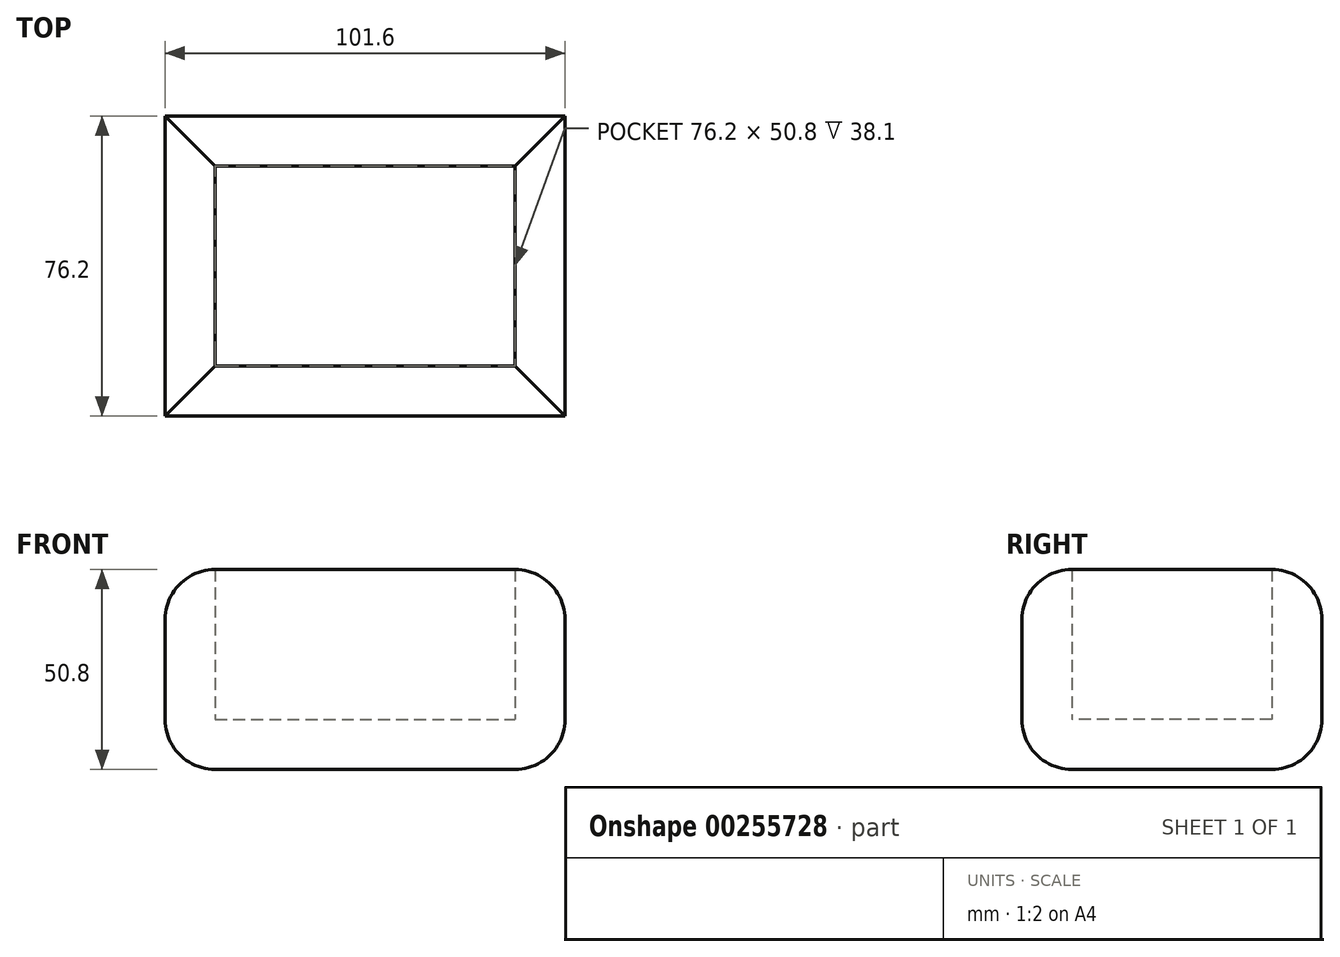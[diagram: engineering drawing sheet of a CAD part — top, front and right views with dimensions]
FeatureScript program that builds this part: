
annotation { "Feature Type Name" : "Feature", "Feature Type Description" : "" }
export const myFeature = defineFeature(function(context is Context, id is Id, definition is map)
    precondition{}
    {
        {
            var Q0;
            Q0=qCreatedBy(makeId("Top.planeOp"),FACE);
            var sketch = newSketch(context, id + "F0", { "sketchPlane" : qUnion([Q0])});
            skLineSegment(sketch, "E0", {"start": v(-52.15, 25.23) * mm, "end": v(49.45, 25.23) * mm});
            skLineSegment(sketch, "E1", {"start": v(49.45, 25.23) * mm, "end": v(49.45, -50.97) * mm});
            skLineSegment(sketch, "E2", {"start": v(49.45, -50.97) * mm, "end": v(-52.15, -50.97) * mm});
            skLineSegment(sketch, "E3", {"start": v(-52.15, -50.97) * mm, "end": v(-52.15, 25.23) * mm});
            skSolve(sketch);
        }
        {
            var Q0;
            Q0=makeQuery(id+"F0.imprint","IMPRINT",FACE,{"disambiguationData":[TD([[makeQuery(id+"F0.imprint","IMPRINT",EDGE,{"derivedFrom":sQuery(id+"F0.wireOp",EDGE,"E0")}),-1.0]])]});
            extrude(context, id + "F1", {"entities" : qUnion([Q0]), "depth" : 50.8 * mm});
        }
        {
            var Q0;
            Q0=makeQuery(id+"F1.opExtrude","CAP_FACE",FACE,{"disambiguationData":[OSD([sQuery(id+"F0.wireOp",EDGE,"E0"),sQuery(id+"F0.wireOp",EDGE,"E1"),sQuery(id+"F0.wireOp",EDGE,"E2"),sQuery(id+"F0.wireOp",EDGE,"E3")])],"isStart":false});
            var Q1;
            Q1=makeQuery(id+"F1.opExtrude","CAP_FACE",FACE,{"disambiguationData":[OSD([sQuery(id+"F0.wireOp",EDGE,"E0"),sQuery(id+"F0.wireOp",EDGE,"E1"),sQuery(id+"F0.wireOp",EDGE,"E2"),sQuery(id+"F0.wireOp",EDGE,"E3")])],"isStart":true});
            fillet(context, id + "F2", {"entities" : qUnion([Q0, Q1]), "radius" : 12.7 * mm, "tangentPropagation" : true, "allowEdgeOverflow" : false});
        }
        {
            var Q0;
            Q0=makeQuery(id+"F1.opExtrude","CAP_FACE",FACE,{"disambiguationData":[OSD([sQuery(id+"F0.wireOp",EDGE,"E0"),sQuery(id+"F0.wireOp",EDGE,"E1"),sQuery(id+"F0.wireOp",EDGE,"E2"),sQuery(id+"F0.wireOp",EDGE,"E3")])],"isStart":false});
            shell(context, id + "F3", {"entities" : qUnion([Q0]), "thickness" : 12.7 * mm});
        }
    });
